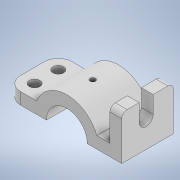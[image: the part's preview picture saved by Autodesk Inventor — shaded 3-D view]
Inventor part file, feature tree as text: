
AUTODESK INVENTOR PART (.ipt)
format: ipt  version: 2022 (Build 260153000, 153)  size: 165,376 bytes
history: native  units: mm
features: extrude x3, sketch x3, fillet x2, other x1
ambient origin geometry x8: Origin, YZ Plane, XZ Plane, XY Plane, X Axis, Y Axis, Z Axis, Center Point
bodies: Body1 (feature_tree)
feature tree (9):
  other  "Sólido1"
  extrude  "Extrusão1"  Depth=41.0mm
  extrude  "Extrusão2"  Depth=107.0mm
  extrude  "Extrusão3"  Depth=48.0mm TaperAngle=0.0deg
  fillet  "Arredondamento1"  Radius=10.0mm
  fillet  "Arredondamento2"  Radius=10.0mm
  sketch  "Esboço1"  dims[d0=38.0mm d5=41.0mm]
  sketch  "Esboço2"  dims[d6=51.0mm d7=107.0mm]
  sketch  "Esboço3"  dims[d8=11.0mm d9=48.0mm d10=0.0mm d11=10.0mm d12=10.0mm d13=22.0mm d14=13.0mm d15=13.0mm d16=5.0mm d17=24.0mm d18=24.0mm d19=27.911mm d20=27.910571mm d21=0.0mm d22=0.0mm d23=13.0mm d24=25.0mm d27=10.0mm d28=0.0mm d29=13.0mm d30=5.0mm]
